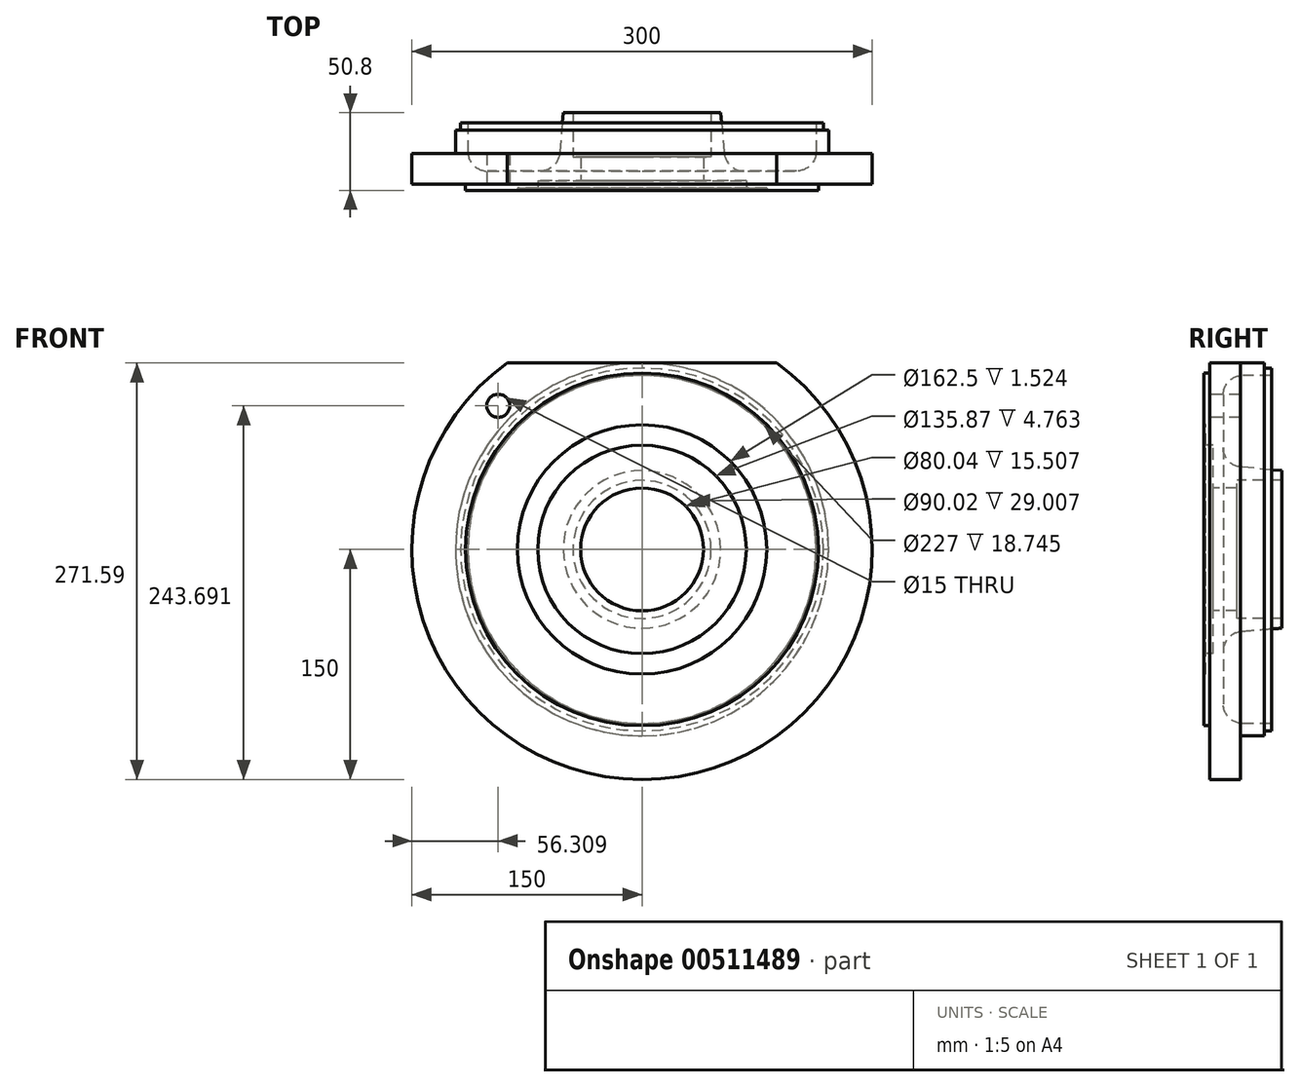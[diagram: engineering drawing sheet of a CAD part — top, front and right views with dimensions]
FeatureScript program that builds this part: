
annotation { "Feature Type Name" : "Feature", "Feature Type Description" : "" }
export const myFeature = defineFeature(function(context is Context, id is Id, definition is map)
    precondition{}
    {
        {
            var Q0;
            Q0=qCreatedBy(makeId("Right.planeOp"),FACE);
            var sketch = newSketch(context, id + "F0", { "sketchPlane" : qUnion([Q0])});
            skLineSegment(sketch, "E0", {"start": v(0, 0) * mm, "end": v(126.94, 0) * mm, "construction": true});
            skLineSegment(sketch, "E1", {"start": v(3.99, 150) * mm, "end": v(23.98, 150) * mm});
            skLineSegment(sketch, "E2", {"start": v(0, 115) * mm, "end": v(3.99, 115) * mm});
            skLineSegment(sketch, "E3", {"start": v(3.99, 115) * mm, "end": v(3.99, 150) * mm});
            skLineSegment(sketch, "E4", {"start": v(23.98, 121.59) * mm, "end": v(39.37, 121.59) * mm});
            skLineSegment(sketch, "E5", {"start": v(23.98, 121.59) * mm, "end": v(23.98, 150) * mm});
            skLineSegment(sketch, "E6", {"start": v(39.37, 121.59) * mm, "end": v(39.37, 118.26) * mm});
            skLineSegment(sketch, "E7", {"start": v(39.37, 118.26) * mm, "end": v(44.15, 118.26) * mm});
            skLineSegment(sketch, "E8", {"start": v(44.15, 118.26) * mm, "end": v(44.15, 113.5) * mm});
            skLineSegment(sketch, "E9", {"start": v(44.15, 113.5) * mm, "end": v(12.7, 113.5) * mm});
            skLineSegment(sketch, "E10", {"start": v(12.7, 113.5) * mm, "end": v(12.7, 54.7) * mm});
            skLineSegment(sketch, "E11", {"start": v(0, 115) * mm, "end": v(0, 81.25) * mm});
            skLineSegment(sketch, "E12", {"start": v(0, 81.25) * mm, "end": v(1.52, 81.25) * mm});
            skLineSegment(sketch, "E13", {"start": v(1.52, 81.25) * mm, "end": v(1.52, 67.93) * mm});
            skLineSegment(sketch, "E14", {"start": v(1.52, 67.93) * mm, "end": v(6.29, 67.93) * mm});
            skLineSegment(sketch, "E15", {"start": v(6.29, 67.93) * mm, "end": v(6.29, 40.02) * mm});
            skLineSegment(sketch, "E16", {"start": v(6.29, 40.02) * mm, "end": v(21.8, 40.02) * mm});
            skLineSegment(sketch, "E17", {"start": v(21.8, 40.02) * mm, "end": v(21.8, 45) * mm});
            skLineSegment(sketch, "E18", {"start": v(21.8, 45) * mm, "end": v(50.8, 45) * mm});
            skLineSegment(sketch, "E19", {"start": v(50.8, 45) * mm, "end": v(50.8, 51.36) * mm});
            skLineSegment(sketch, "E20", {"start": v(50.8, 51.36) * mm, "end": v(12.7, 54.7) * mm});
            skSolve(sketch);
        }
        {
            var Q0;
            Q0=makeQuery(id+"F0.imprint","IMPRINT",FACE,{"disambiguationData":[TD([[makeQuery(id+"F0.imprint","IMPRINT",EDGE,{"derivedFrom":sQuery(id+"F0.wireOp",EDGE,"E1")}),-1.0]])]});
            var Q1;
            Q1=sQuery(id+"F0.wireOp",EDGE,"E0");
            revolve(context, id + "F1", {"entities" : qUnion([Q0]), "axis" : qUnion([Q1]), "revolveType" : RevolveType.FULL});
        }
        {
            var Q0;
            Q0=makeQuery(id+"F1.opRevolve","SWEPT_FACE",FACE,{"disambiguationData":[OSD([sQuery(id+"F0.wireOp",EDGE,"E3")])]});
            var sketch = newSketch(context, id + "F2", { "sketchPlane" : qUnion([Q0])});
            skLineSegment(sketch, "E21", {"start": v(0, 0) * mm, "end": v(-163.96, 0) * mm, "construction": true});
            skLineSegment(sketch, "E22", {"start": v(0, 0) * mm, "end": v(-129.92, 129.92) * mm, "construction": true});
            skCircle(sketch, "E23", {"center": v(0, 0) * mm, "radius": 132.5 * mm, "construction": true});
            skCircle(sketch, "E24", {"center": v(-93.7, 93.7) * mm, "radius": 7.5 * mm});
            skLineSegment(sketch, "E25", {"start": v(-111.02, 121.59) * mm, "end": v(147.7, 121.59) * mm});
            skLineSegment(sketch, "E26", {"start": v(147.7, 121.59) * mm, "end": v(147.7, 169.05) * mm});
            skLineSegment(sketch, "E27", {"start": v(147.7, 169.05) * mm, "end": v(-111.02, 169.05) * mm});
            skLineSegment(sketch, "E28", {"start": v(-111.02, 169.05) * mm, "end": v(-111.02, 121.59) * mm});
            skSolve(sketch);
        }
        {
            var Q0;
            Q0=makeQuery(id+"F2.imprint","IMPRINT",FACE,{"disambiguationData":[TD([[makeQuery(id+"F2.imprint","IMPRINT",EDGE,{"derivedFrom":sQuery(id+"F2.wireOp",EDGE,"E24")}),1.0]])]});
            var Q1;
            {var subQ0=sQuery(id+"F2.wireOp",EDGE,"E26");Q1=makeQuery(id+"F2.imprint","IMPRINT",FACE,{"disambiguationData":[TD([[makeQuery(id+"F2.imprint","IMPRINT",EDGE,{"derivedFrom":subQ0}),1.0]])]});}
            var Q2;
            {var subQ0=sQuery(id+"F2.wireOp",EDGE,"E25");var subQ1=makeQuery(id+"F1.opRevolve","SWEPT_EDGE",EDGE,{"disambiguationData":[OSD([sQuery(id+"F0.wireOp",EDGE,"E1"),sQuery(id+"F0.wireOp",EDGE,"E3")])]});var subQ2=makeQuery(id+"F2.imprint","INTERSECT",VERTEX,{"disambiguationData":[OD(0.0)],"derivedFrom":[subQ1,subQ0]});Q2=makeQuery(id+"F2.imprint","IMPRINT",FACE,{"disambiguationData":[TD([[makeQuery(id+"F2.imprint","IMPRINT",EDGE,{"disambiguationData":[TD([[subQ2,-1.0]])],"derivedFrom":subQ0}),1.0]])]});}
            extrude(context, id + "F3", {"entities" : qUnion([Q0, Q1, Q2]), "operationType" : NewBodyOperationType.REMOVE, "oppositeDirection" : true, "depth" : 25.4 * mm});
        }
        {
            var Q0;
            Q0=makeQuery(id+"F1.opRevolve","SWEPT_EDGE",EDGE,{"disambiguationData":[OSD([sQuery(id+"F0.wireOp",EDGE,"E9"),sQuery(id+"F0.wireOp",EDGE,"E10")])]});
            var Q1;
            Q1=makeQuery(id+"F1.opRevolve","SWEPT_EDGE",EDGE,{"disambiguationData":[OSD([sQuery(id+"F0.wireOp",EDGE,"E10"),sQuery(id+"F0.wireOp",EDGE,"E20")])]});
            fillet(context, id + "F4", {"entities" : qUnion([Q0, Q1]), "radius" : 12.7 * mm, "tangentPropagation" : true, "allowEdgeOverflow" : false});
        }
    });
